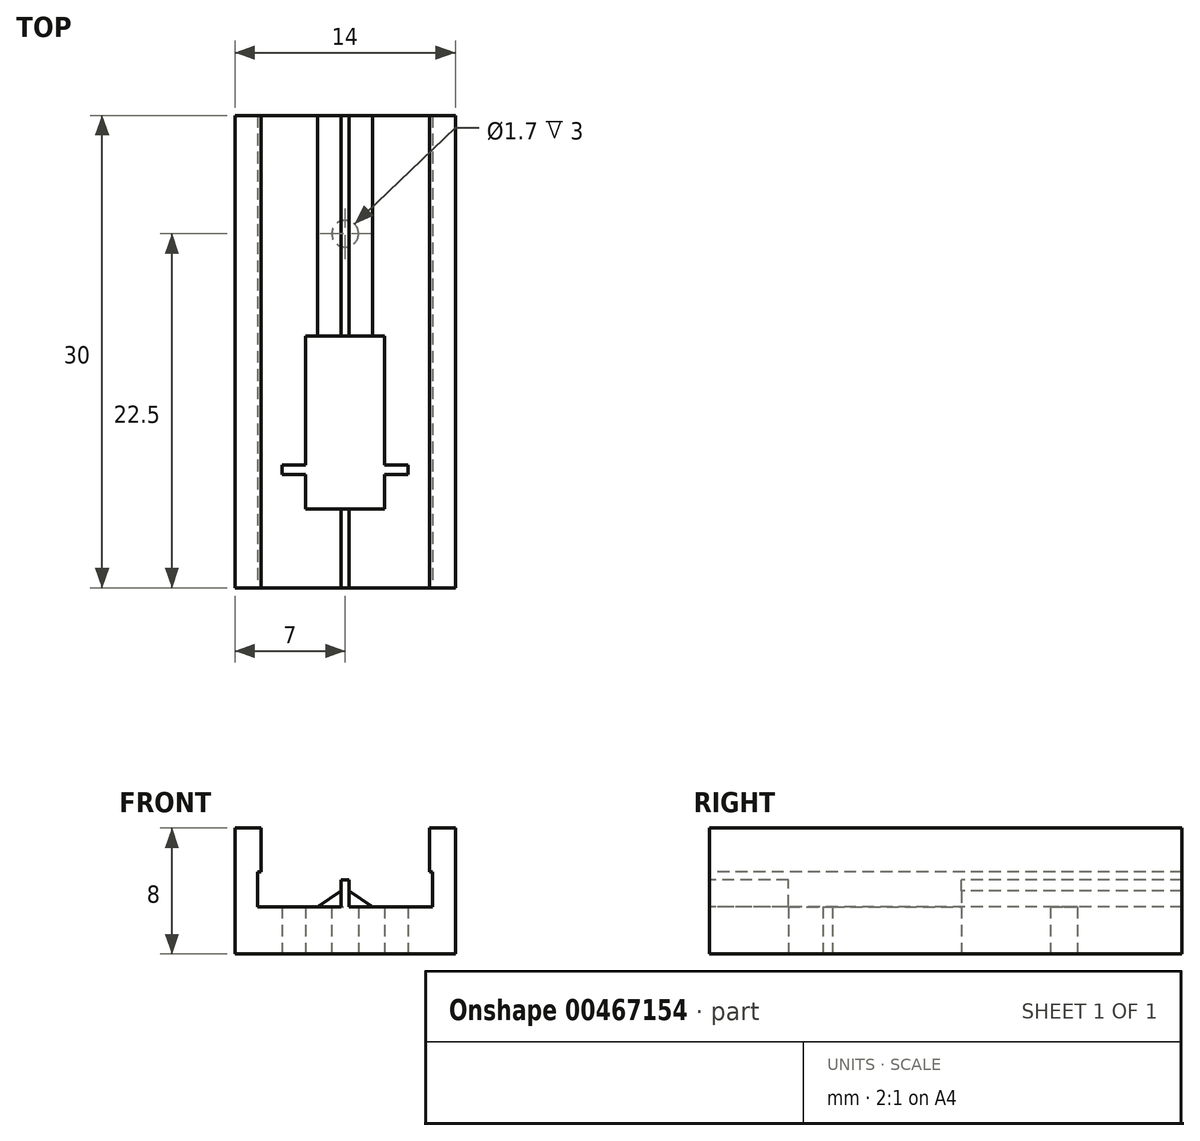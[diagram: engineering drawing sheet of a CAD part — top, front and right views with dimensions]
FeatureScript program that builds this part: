
annotation { "Feature Type Name" : "Feature", "Feature Type Description" : "" }
export const myFeature = defineFeature(function(context is Context, id is Id, definition is map)
    precondition{}
    {
        {
            var Q0;
            Q0=qCreatedBy(makeId("Front.planeOp"),FACE);
            var sketch = newSketch(context, id + "F0", { "sketchPlane" : qUnion([Q0])});
            skLineSegment(sketch, "E0.bottom", {"start": v(-7, 4) * mm, "end": v(7, 4) * mm});
            skLineSegment(sketch, "E0.top", {"start": v(-7, -4) * mm, "end": v(7, -4) * mm});
            skLineSegment(sketch, "E0.left", {"start": v(-7, 4) * mm, "end": v(-7, -4) * mm});
            skLineSegment(sketch, "E0.right", {"start": v(7, 4) * mm, "end": v(7, -4) * mm});
            skSolve(sketch);
        }
        {
            var Q0;
            Q0=makeQuery(id+"F0.imprint","IMPRINT",FACE,{"disambiguationData":[TD([[makeQuery(id+"F0.imprint","IMPRINT",EDGE,{"derivedFrom":sQuery(id+"F0.wireOp",EDGE,"E0.bottom")}),-1.0]])]});
            extrude(context, id + "F1", {"entities" : qUnion([Q0]), "depth" : 30 * mm});
        }
        {
            var Q0;
            Q0=makeQuery(id+"F1.opExtrude","CAP_FACE",FACE,{"disambiguationData":[OSD([sQuery(id+"F0.wireOp",EDGE,"E0.bottom"),sQuery(id+"F0.wireOp",EDGE,"E0.top"),sQuery(id+"F0.wireOp",EDGE,"E0.left"),sQuery(id+"F0.wireOp",EDGE,"E0.right")])],"isStart":false});
            var sketch = newSketch(context, id + "F2", { "sketchPlane" : qUnion([Q0])});
            skLineSegment(sketch, "E1.top", {"start": v(-0.25, 0.7) * mm, "end": v(0.25, 0.7) * mm});
            skLineSegment(sketch, "E1.left", {"start": v(-0.25, 0) * mm, "end": v(-0.25, 0.7) * mm});
            skLineSegment(sketch, "E1.right", {"start": v(0.25, 0) * mm, "end": v(0.25, 0.7) * mm});
            skLineSegment(sketch, "E2", {"start": v(-1.75, -1) * mm, "end": v(-0.25, 0) * mm});
            skLineSegment(sketch, "E3", {"start": v(0.25, 0) * mm, "end": v(1.75, -1) * mm});
            skLineSegment(sketch, "E4.bottom", {"start": v(-5.35, 1.2) * mm, "end": v(-5.55, 1.2) * mm});
            skLineSegment(sketch, "E4.right", {"start": v(-5.55, 1.2) * mm, "end": v(-5.55, -1) * mm});
            skLineSegment(sketch, "E5.top", {"start": v(5.35, 1.2) * mm, "end": v(5.55, 1.2) * mm});
            skLineSegment(sketch, "E5.right", {"start": v(5.55, -1) * mm, "end": v(5.55, 1.2) * mm});
            skLineSegment(sketch, "E6", {"start": v(-5.55, -1) * mm, "end": v(-1.75, -1) * mm});
            skLineSegment(sketch, "E7", {"start": v(1.75, -1) * mm, "end": v(5.55, -1) * mm});
            skLineSegment(sketch, "E8", {"start": v(-5.35, 1.2) * mm, "end": v(-5.35, 4) * mm});
            skLineSegment(sketch, "E9", {"start": v(5.35, 1.2) * mm, "end": v(5.35, 4) * mm});
            skSolve(sketch);
        }
        {
            var Q0;
            Q0=makeQuery(id+"F1.opExtrude","SWEPT_FACE",FACE,{"disambiguationData":[OSD([sQuery(id+"F0.wireOp",EDGE,"E0.top")])]});
            var sketch = newSketch(context, id + "F3", { "sketchPlane" : qUnion([Q0])});
            skLineSegment(sketch, "E10.bottom", {"start": v(2.5, 14) * mm, "end": v(-2.5, 14) * mm});
            skLineSegment(sketch, "E10.top", {"start": v(2.5, 25) * mm, "end": v(-2.5, 25) * mm});
            skLineSegment(sketch, "E10.left", {"start": v(2.5, 14) * mm, "end": v(2.5, 25) * mm});
            skLineSegment(sketch, "E10.right", {"start": v(-2.5, 14) * mm, "end": v(-2.5, 25) * mm});
            skLineSegment(sketch, "E11.bottom", {"start": v(-2.5, 22.2) * mm, "end": v(-4, 22.2) * mm});
            skLineSegment(sketch, "E11.top", {"start": v(-2.5, 22.8) * mm, "end": v(-4, 22.8) * mm});
            skLineSegment(sketch, "E11.left", {"start": v(-2.5, 22.2) * mm, "end": v(-2.5, 22.8) * mm});
            skLineSegment(sketch, "E11.right", {"start": v(-4, 22.2) * mm, "end": v(-4, 22.8) * mm});
            skLineSegment(sketch, "E12.bottom", {"start": v(2.5, 22.2) * mm, "end": v(4, 22.2) * mm});
            skLineSegment(sketch, "E12.top", {"start": v(2.5, 22.8) * mm, "end": v(4, 22.8) * mm});
            skLineSegment(sketch, "E12.left", {"start": v(2.5, 22.2) * mm, "end": v(2.5, 22.8) * mm});
            skLineSegment(sketch, "E12.right", {"start": v(4, 22.2) * mm, "end": v(4, 22.8) * mm});
            skSolve(sketch);
        }
        {
            var Q0;
            {var subQ2=sQuery(id+"F3.wireOp",EDGE,"E12.bottom");Q0=makeQuery(id+"F3.imprint","IMPRINT",FACE,{"disambiguationData":[TD([[makeQuery(id+"F3.imprint","IMPRINT",EDGE,{"derivedFrom":subQ2}),1.0]])]});}
            var Q1;
            {var subQ3=sQuery(id+"F3.wireOp",EDGE,"E10.bottom");Q1=makeQuery(id+"F3.imprint","IMPRINT",FACE,{"disambiguationData":[TD([[makeQuery(id+"F3.imprint","IMPRINT",EDGE,{"derivedFrom":subQ3}),-1.0]])]});}
            var Q2;
            Q2=makeQuery(id+"F3.imprint","IMPRINT",FACE,{"disambiguationData":[TD([[makeQuery(id+"F3.imprint","IMPRINT",EDGE,{"derivedFrom":sQuery(id+"F3.wireOp",EDGE,"6ZGtiWLi-mccN-Tt0I-NmYB-gDmVxvnO52zQ.bottom")}),1.0]])]});
            var Q3;
            {var subQ2=sQuery(id+"F3.wireOp",EDGE,"E11.bottom");Q3=makeQuery(id+"F3.imprint","IMPRINT",FACE,{"disambiguationData":[TD([[makeQuery(id+"F3.imprint","IMPRINT",EDGE,{"derivedFrom":subQ2}),-1.0]])]});}
            var Q4;
            Q4=makeQuery(id+"F1.opExtrude","SWEPT_FACE",FACE,{"disambiguationData":[OSD([sQuery(id+"F0.wireOp",EDGE,"E0.bottom")])]});
            extrude(context, id + "F4", {"entities" : qUnion([Q0, Q1, Q2, Q3]), "operationType" : NewBodyOperationType.REMOVE, "endBound" : BoundingType.UP_TO_SURFACE, "oppositeDirection" : true, "endBoundEntityFace" : qUnion([Q4]), "depth" : 25 * mm});
        }
        {
            var Q0;
            Q0=makeQuery(id+"F2.imprint","IMPRINT",FACE,{"disambiguationData":[TD([[makeQuery(id+"F2.imprint","IMPRINT",EDGE,{"derivedFrom":sQuery(id+"F2.wireOp",EDGE,"E1.top")}),1.0]])]});
            extrude(context, id + "F5", {"entities" : qUnion([Q0]), "operationType" : NewBodyOperationType.REMOVE, "endBound" : BoundingType.THROUGH_ALL, "oppositeDirection" : true, "depth" : 25 * mm});
        }
        {
            var Q0;
            Q0=makeQuery(id+"F1.opExtrude","CAP_FACE",FACE,{"disambiguationData":[OSD([sQuery(id+"F0.wireOp",EDGE,"E0.bottom"),sQuery(id+"F0.wireOp",EDGE,"E0.top"),sQuery(id+"F0.wireOp",EDGE,"E0.left"),sQuery(id+"F0.wireOp",EDGE,"E0.right")])],"isStart":false});
            var sketch = newSketch(context, id + "F6", { "sketchPlane" : qUnion([Q0])});
            skLineSegment(sketch, "E13.bottom", {"start": v(-0.25, 0) * mm, "end": v(-1.75, 0) * mm});
            skLineSegment(sketch, "E13.top", {"start": v(-0.25, -1) * mm, "end": v(-1.75, -1) * mm});
            skLineSegment(sketch, "E13.left", {"start": v(-0.25, 0) * mm, "end": v(-0.25, -1) * mm});
            skLineSegment(sketch, "E13.right", {"start": v(-1.75, 0) * mm, "end": v(-1.75, -1) * mm});
            skLineSegment(sketch, "E14.bottom", {"start": v(0.25, 0) * mm, "end": v(1.75, 0) * mm});
            skLineSegment(sketch, "E14.top", {"start": v(0.25, -1) * mm, "end": v(1.75, -1) * mm});
            skLineSegment(sketch, "E14.left", {"start": v(0.25, 0) * mm, "end": v(0.25, -1) * mm});
            skLineSegment(sketch, "E14.right", {"start": v(1.75, 0) * mm, "end": v(1.75, -1) * mm});
            skSolve(sketch);
        }
        {
            var Q0;
            Q0=makeQuery(id+"F6.imprint","IMPRINT",FACE,{"disambiguationData":[TD([[makeQuery(id+"F6.imprint","IMPRINT",EDGE,{"derivedFrom":sQuery(id+"F6.wireOp",EDGE,"E13.top")}),-1.0]])]});
            var Q1;
            Q1=makeQuery(id+"F6.imprint","IMPRINT",FACE,{"disambiguationData":[TD([[makeQuery(id+"F6.imprint","IMPRINT",EDGE,{"derivedFrom":sQuery(id+"F6.wireOp",EDGE,"E14.top")}),1.0]])]});
            var Q2;
            Q2=makeQuery(id+"F4.boolean.opBoolean","COPY",FACE,{"derivedFrom":makeQuery(id+"F4.opExtrude","SWEPT_FACE",FACE,{"disambiguationData":[OSD([sQuery(id+"F3.wireOp",EDGE,"E10.top")])]})});
            extrude(context, id + "F7", {"entities" : qUnion([Q0, Q1]), "operationType" : NewBodyOperationType.REMOVE, "endBound" : BoundingType.UP_TO_SURFACE, "oppositeDirection" : true, "endBoundEntityFace" : qUnion([Q2]), "depth" : 25 * mm});
        }
        {
            var Q0;
            Q0=makeQuery(id+"F1.opExtrude","SWEPT_FACE",FACE,{"disambiguationData":[OSD([sQuery(id+"F0.wireOp",EDGE,"E0.top")])]});
            var sketch = newSketch(context, id + "F8", { "sketchPlane" : qUnion([Q0])});
            skCircle(sketch, "E15", {"center": v(0, 7.5) * mm, "radius": 0.85 * mm});
            skSolve(sketch);
        }
        {
            var Q0;
            Q0=makeQuery(id+"F8.imprint","IMPRINT",FACE,{"disambiguationData":[TD([[makeQuery(id+"F8.imprint","IMPRINT",EDGE,{"derivedFrom":sQuery(id+"F8.wireOp",EDGE,"E15")}),1.0]])]});
            extrude(context, id + "F9", {"entities" : qUnion([Q0]), "operationType" : NewBodyOperationType.REMOVE, "oppositeDirection" : true, "depth" : 3 * mm});
        }
    });
